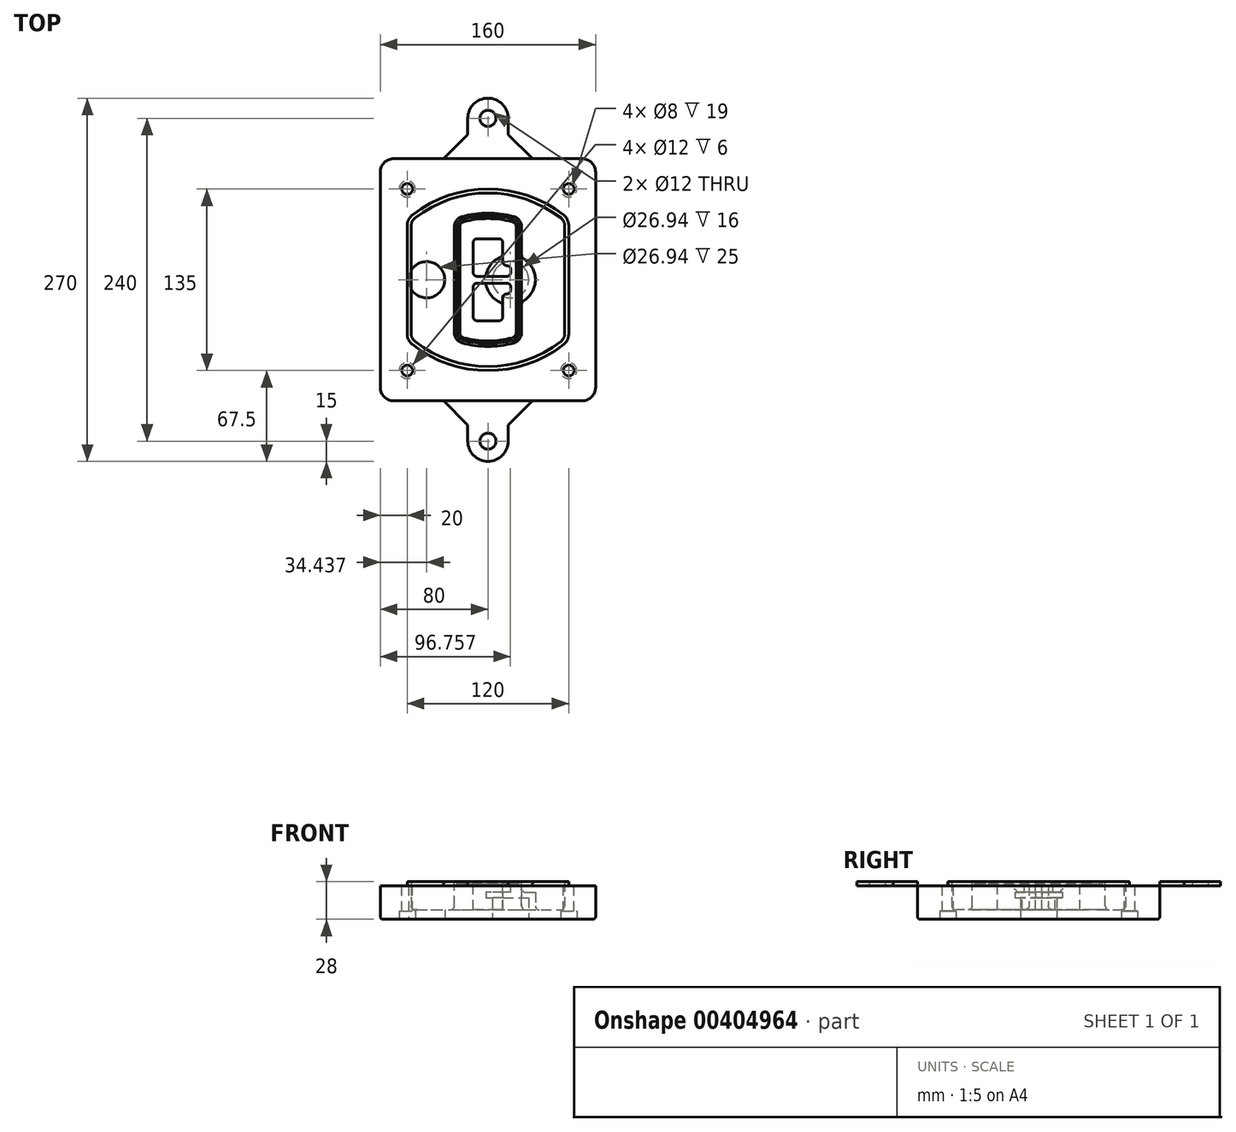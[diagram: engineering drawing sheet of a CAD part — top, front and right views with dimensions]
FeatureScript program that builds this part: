
annotation { "Feature Type Name" : "Feature", "Feature Type Description" : "" }
export const myFeature = defineFeature(function(context is Context, id is Id, definition is map)
    precondition{}
    {
        {
            var Q0;
            Q0=qCreatedBy(makeId("Top.planeOp"),FACE);
            var sketch = newSketch(context, id + "F0", { "sketchPlane" : qUnion([Q0])});
            skPoint(sketch, "E0.rect.middle", {"position": v(0, 0) * mm});
            skLineSegment(sketch, "E1.bottom", {"start": v(-70, -90) * mm, "end": v(70, -90) * mm});
            skLineSegment(sketch, "E1.top", {"start": v(-70, 90) * mm, "end": v(70, 90) * mm});
            skLineSegment(sketch, "E1.left", {"start": v(-80, -80) * mm, "end": v(-80, 80) * mm});
            skLineSegment(sketch, "E1.right", {"start": v(80, -80) * mm, "end": v(80, 80) * mm});
            skLineSegment(sketch, "E2", {"start": v(-80, 90) * mm, "end": v(80, -90) * mm, "construction": true});
            skLineSegment(sketch, "E3", {"start": v(80, 90) * mm, "end": v(-80, -90) * mm, "construction": true});
            skCircle(sketch, "E4", {"center": v(-60, 67.5) * mm, "radius": 4 * mm});
            skCircle(sketch, "E5", {"center": v(60, 67.5) * mm, "radius": 4 * mm});
            skCircle(sketch, "E6", {"center": v(60, -67.5) * mm, "radius": 4 * mm});
            skCircle(sketch, "E7", {"center": v(-60, -67.5) * mm, "radius": 4 * mm});
            skLineSegment(sketch, "E8", {"start": v(-60, 67.5) * mm, "end": v(60, 67.5) * mm, "construction": true});
            skLineSegment(sketch, "E9", {"start": v(60, 67.5) * mm, "end": v(60, -67.5) * mm, "construction": true});
            skLineSegment(sketch, "E10", {"start": v(60, -67.5) * mm, "end": v(-60, -67.5) * mm, "construction": true});
            skLineSegment(sketch, "E11", {"start": v(-60, -67.5) * mm, "end": v(-60, 67.5) * mm, "construction": true});
            skLineSegment(sketch, "E12", {"start": v(-60, 40.3) * mm, "end": v(-60, -40.3) * mm});
            skLineSegment(sketch, "E13", {"start": v(60, 40.3) * mm, "end": v(60, -40.3) * mm});
            skArc(sketch, "E14", {"start": v(56.15, 48.18) * mm, "mid": v(0, 67.5) * mm, "end": v(-56.15, 48.18) * mm});
            skArc(sketch, "E15", {"start": v(-56.15, -48.18) * mm, "mid": v(0, -67.5) * mm, "end": v(56.15, -48.18) * mm});
            skLineSegment(sketch, "E16", {"start": v(-60, 0) * mm, "end": v(60, 0) * mm, "construction": true});
            skPoint(sketch, "E17.visualSharp", {"position": v(-60, -45) * mm});
            skArc(sketch, "E17.filletArc", {"start": v(-60, -40.3) * mm, "mid": v(-58.99, -44.68) * mm, "end": v(-56.15, -48.18) * mm});
            skPoint(sketch, "E18.visualSharp", {"position": v(-60, 45) * mm});
            skArc(sketch, "E18.filletArc", {"start": v(-56.15, 48.18) * mm, "mid": v(-58.99, 44.68) * mm, "end": v(-60, 40.3) * mm});
            skPoint(sketch, "E19.visualSharp", {"position": v(60, 45) * mm});
            skArc(sketch, "E19.filletArc", {"start": v(60, 40.3) * mm, "mid": v(58.99, 44.68) * mm, "end": v(56.15, 48.18) * mm});
            skPoint(sketch, "E20.visualSharp", {"position": v(60, -45) * mm});
            skArc(sketch, "E20.filletArc", {"start": v(56.15, -48.18) * mm, "mid": v(58.99, -44.68) * mm, "end": v(60, -40.3) * mm});
            skPoint(sketch, "E21.visualSharp", {"position": v(-80, 90) * mm});
            skArc(sketch, "E21.filletArc", {"start": v(-70, 90) * mm, "mid": v(-77.07, 87.07) * mm, "end": v(-80, 80) * mm});
            skPoint(sketch, "E22.visualSharp", {"position": v(80, 90) * mm});
            skArc(sketch, "E22.filletArc", {"start": v(80, 80) * mm, "mid": v(77.07, 87.07) * mm, "end": v(70, 90) * mm});
            skPoint(sketch, "E23.visualSharp", {"position": v(80, -90) * mm});
            skArc(sketch, "E23.filletArc", {"start": v(70, -90) * mm, "mid": v(77.07, -87.07) * mm, "end": v(80, -80) * mm});
            skPoint(sketch, "E24.visualSharp", {"position": v(-80, -90) * mm});
            skArc(sketch, "E24.filletArc", {"start": v(-80, -80) * mm, "mid": v(-77.07, -87.07) * mm, "end": v(-70, -90) * mm});
            skArc(sketch, "E25.0", {"start": v(57, 40.3) * mm, "mid": v(56.3, 43.36) * mm, "end": v(54.3, 45.81) * mm});
            skLineSegment(sketch, "E25.1", {"start": v(57, 40.3) * mm, "end": v(57, -40.3) * mm});
            skArc(sketch, "E25.2", {"start": v(54.3, -45.81) * mm, "mid": v(56.3, -43.36) * mm, "end": v(57, -40.3) * mm});
            skArc(sketch, "E25.3", {"start": v(-54.3, -45.81) * mm, "mid": v(0, -64.5) * mm, "end": v(54.3, -45.81) * mm});
            skArc(sketch, "E25.4", {"start": v(-57, -40.3) * mm, "mid": v(-56.3, -43.36) * mm, "end": v(-54.3, -45.81) * mm});
            skArc(sketch, "E25.5", {"start": v(54.3, 45.81) * mm, "mid": v(0, 64.5) * mm, "end": v(-54.3, 45.81) * mm});
            skLineSegment(sketch, "E25.6", {"start": v(-57, 40.3) * mm, "end": v(-57, -40.3) * mm});
            skArc(sketch, "E25.7", {"start": v(-54.3, 45.81) * mm, "mid": v(-56.3, 43.36) * mm, "end": v(-57, 40.3) * mm});
            skArc(sketch, "E26.0", {"start": v(-58.62, 51.33) * mm, "mid": v(-62.58, 46.43) * mm, "end": v(-64, 40.3) * mm});
            skArc(sketch, "E26.1", {"start": v(58.62, 51.33) * mm, "mid": v(0, 71.5) * mm, "end": v(-58.62, 51.33) * mm});
            skArc(sketch, "E26.2", {"start": v(64, 40.3) * mm, "mid": v(62.58, 46.43) * mm, "end": v(58.62, 51.33) * mm});
            skLineSegment(sketch, "E26.3", {"start": v(64, 40.3) * mm, "end": v(64, -40.3) * mm});
            skArc(sketch, "E26.4", {"start": v(58.62, -51.33) * mm, "mid": v(62.58, -46.43) * mm, "end": v(64, -40.3) * mm});
            skLineSegment(sketch, "E26.5", {"start": v(-64, 40.3) * mm, "end": v(-64, -40.3) * mm});
            skArc(sketch, "E26.6", {"start": v(-58.62, -51.33) * mm, "mid": v(0, -71.5) * mm, "end": v(58.62, -51.33) * mm});
            skArc(sketch, "E26.7", {"start": v(-64, -40.3) * mm, "mid": v(-62.58, -46.43) * mm, "end": v(-58.62, -51.33) * mm});
            skSolve(sketch);
        }
        {
            var Q0;
            Q0=makeQuery(id+"F0.imprint","IMPRINT",FACE,{"disambiguationData":[TD([[makeQuery(id+"F0.imprint","IMPRINT",EDGE,{"derivedFrom":sQuery(id+"F0.wireOp",EDGE,"E1.bottom")}),1.0]])]});
            var Q1;
            Q1=makeQuery(id+"F0.imprint","IMPRINT",FACE,{"disambiguationData":[TD([[makeQuery(id+"F0.imprint","IMPRINT",EDGE,{"derivedFrom":sQuery(id+"F0.wireOp",EDGE,"E12")}),1.0]])]});
            var Q2;
            Q2=makeQuery(id+"F0.imprint","IMPRINT",FACE,{"disambiguationData":[TD([[makeQuery(id+"F0.imprint","IMPRINT",EDGE,{"derivedFrom":sQuery(id+"F0.wireOp",EDGE,"E25.0")}),1.0]])]});
            var Q3;
            Q3=makeQuery(id+"F0.imprint","IMPRINT",FACE,{"disambiguationData":[TD([[makeQuery(id+"F0.imprint","IMPRINT",EDGE,{"derivedFrom":sQuery(id+"F0.wireOp",EDGE,"E12")}),-1.0]])]});
            extrude(context, id + "F1", {"entities" : qUnion([Q0, Q1, Q2, Q3]), "oppositeDirection" : true, "depth" : 25 * mm});
        }
        {
            var Q0;
            Q0=makeQuery(id+"F0.imprint","IMPRINT",FACE,{"disambiguationData":[TD([[makeQuery(id+"F0.imprint","IMPRINT",EDGE,{"derivedFrom":sQuery(id+"F0.wireOp",EDGE,"E12")}),1.0]])]});
            extrude(context, id + "F2", {"entities" : qUnion([Q0]), "operationType" : NewBodyOperationType.ADD, "depth" : 3 * mm});
        }
        {
            var Q0;
            Q0=makeQuery(id+"F0.imprint","IMPRINT",FACE,{"disambiguationData":[TD([[makeQuery(id+"F0.imprint","IMPRINT",EDGE,{"derivedFrom":sQuery(id+"F0.wireOp",EDGE,"E25.0")}),1.0]])]});
            extrude(context, id + "F3", {"entities" : qUnion([Q0]), "operationType" : NewBodyOperationType.REMOVE, "oppositeDirection" : true, "depth" : 18 * mm});
        }
        {
            var Q0;
            Q0=makeQuery(id+"F2.opExtrude","CAP_FACE",FACE,{"disambiguationData":[OSD([sQuery(id+"F0.wireOp",EDGE,"E12"),sQuery(id+"F0.wireOp",EDGE,"E13"),sQuery(id+"F0.wireOp",EDGE,"E14"),sQuery(id+"F0.wireOp",EDGE,"E15"),sQuery(id+"F0.wireOp",EDGE,"E17.filletArc"),sQuery(id+"F0.wireOp",EDGE,"E18.filletArc"),sQuery(id+"F0.wireOp",EDGE,"E19.filletArc"),sQuery(id+"F0.wireOp",EDGE,"E20.filletArc"),sQuery(id+"F0.wireOp",EDGE,"E25.0"),sQuery(id+"F0.wireOp",EDGE,"E25.1"),sQuery(id+"F0.wireOp",EDGE,"E25.2"),sQuery(id+"F0.wireOp",EDGE,"E25.3"),sQuery(id+"F0.wireOp",EDGE,"E25.4"),sQuery(id+"F0.wireOp",EDGE,"E25.5"),sQuery(id+"F0.wireOp",EDGE,"E25.6"),sQuery(id+"F0.wireOp",EDGE,"E25.7")])],"isStart":false});
            var sketch = newSketch(context, id + "F4", { "sketchPlane" : qUnion([Q0])});
            skArc(sketch, "E27.0", {"start": v(-19.08, -46.97) * mm, "mid": v(0, -49.5) * mm, "end": v(19.08, -46.97) * mm});
            skArc(sketch, "E28.0", {"start": v(19.08, 46.97) * mm, "mid": v(0, 49.5) * mm, "end": v(-19.08, 46.97) * mm});
            skLineSegment(sketch, "E29", {"start": v(-25, 39.25) * mm, "end": v(-25, -39.25) * mm});
            skLineSegment(sketch, "E30", {"start": v(25, 39.25) * mm, "end": v(25, -39.25) * mm});
            skLineSegment(sketch, "E31", {"start": v(-25, 45.1) * mm, "end": v(25, 45.1) * mm, "construction": true});
            skLineSegment(sketch, "E32", {"start": v(-25, -45.1) * mm, "end": v(25, -45.1) * mm, "construction": true});
            skPoint(sketch, "E33.visualSharp", {"position": v(-25, 45.1) * mm});
            skArc(sketch, "E33.filletArc", {"start": v(-19.08, 46.97) * mm, "mid": v(-23.35, 44.11) * mm, "end": v(-25, 39.25) * mm});
            skPoint(sketch, "E34.visualSharp", {"position": v(25, 45.1) * mm});
            skArc(sketch, "E34.filletArc", {"start": v(25, 39.25) * mm, "mid": v(23.35, 44.11) * mm, "end": v(19.08, 46.97) * mm});
            skPoint(sketch, "E35.visualSharp", {"position": v(25, -45.1) * mm});
            skArc(sketch, "E35.filletArc", {"start": v(19.08, -46.97) * mm, "mid": v(23.35, -44.11) * mm, "end": v(25, -39.25) * mm});
            skPoint(sketch, "E36.visualSharp", {"position": v(-25, -45.1) * mm});
            skArc(sketch, "E36.filletArc", {"start": v(-25, -39.25) * mm, "mid": v(-23.35, -44.11) * mm, "end": v(-19.08, -46.97) * mm});
            skArc(sketch, "E37.0", {"start": v(54.3, 45.81) * mm, "mid": v(0, 64.5) * mm, "end": v(-54.3, 45.81) * mm});
            skArc(sketch, "E37.1", {"start": v(-54.3, 45.81) * mm, "mid": v(-56.3, 43.36) * mm, "end": v(-57, 40.3) * mm});
            skLineSegment(sketch, "E37.2", {"start": v(-57, 40.3) * mm, "end": v(-57, -40.3) * mm});
            skArc(sketch, "E37.3", {"start": v(-57, -40.3) * mm, "mid": v(-56.3, -43.36) * mm, "end": v(-54.3, -45.81) * mm});
            skArc(sketch, "E37.4", {"start": v(-54.3, -45.81) * mm, "mid": v(0, -64.5) * mm, "end": v(54.3, -45.81) * mm});
            skArc(sketch, "E37.5", {"start": v(54.3, -45.81) * mm, "mid": v(56.3, -43.36) * mm, "end": v(57, -40.3) * mm});
            skLineSegment(sketch, "E37.6", {"start": v(57, 40.3) * mm, "end": v(57, -40.3) * mm});
            skArc(sketch, "E37.7", {"start": v(57, 40.3) * mm, "mid": v(56.3, 43.36) * mm, "end": v(54.3, 45.81) * mm});
            skLineSegment(sketch, "E38.0", {"start": v(23, 39.25) * mm, "end": v(23, -39.25) * mm});
            skArc(sketch, "E38.1", {"start": v(18.56, -45.04) * mm, "mid": v(21.76, -42.9) * mm, "end": v(23, -39.25) * mm});
            skArc(sketch, "E38.2", {"start": v(-18.56, -45.04) * mm, "mid": v(0, -47.5) * mm, "end": v(18.56, -45.04) * mm});
            skArc(sketch, "E38.3", {"start": v(-23, -39.25) * mm, "mid": v(-21.76, -42.9) * mm, "end": v(-18.56, -45.04) * mm});
            skLineSegment(sketch, "E38.4", {"start": v(-23, 39.25) * mm, "end": v(-23, -39.25) * mm});
            skArc(sketch, "E38.5", {"start": v(23, 39.25) * mm, "mid": v(21.76, 42.9) * mm, "end": v(18.56, 45.04) * mm});
            skArc(sketch, "E38.6", {"start": v(-18.56, 45.04) * mm, "mid": v(-21.76, 42.9) * mm, "end": v(-23, 39.25) * mm});
            skArc(sketch, "E38.7", {"start": v(18.56, 45.04) * mm, "mid": v(0, 47.5) * mm, "end": v(-18.56, 45.04) * mm});
            skArc(sketch, "E39.0", {"start": v(21, 39.25) * mm, "mid": v(20.18, 41.68) * mm, "end": v(18.04, 43.1) * mm});
            skLineSegment(sketch, "E39.1", {"start": v(21, 39.25) * mm, "end": v(21, -39.25) * mm});
            skArc(sketch, "E39.2", {"start": v(18.04, -43.1) * mm, "mid": v(20.18, -41.68) * mm, "end": v(21, -39.25) * mm});
            skArc(sketch, "E39.3", {"start": v(-18.04, -43.1) * mm, "mid": v(0, -45.5) * mm, "end": v(18.04, -43.1) * mm});
            skArc(sketch, "E39.4", {"start": v(-21, -39.25) * mm, "mid": v(-20.18, -41.68) * mm, "end": v(-18.04, -43.1) * mm});
            skArc(sketch, "E39.5", {"start": v(18.04, 43.1) * mm, "mid": v(0, 45.5) * mm, "end": v(-18.04, 43.1) * mm});
            skLineSegment(sketch, "E39.6", {"start": v(-21, 39.25) * mm, "end": v(-21, -39.25) * mm});
            skArc(sketch, "E39.7", {"start": v(-18.04, 43.1) * mm, "mid": v(-20.18, 41.68) * mm, "end": v(-21, 39.25) * mm});
            skLineSegment(sketch, "E40", {"start": v(-25, 0) * mm, "end": v(25, 0) * mm, "construction": true});
            skLineSegment(sketch, "E41", {"start": v(-11, 5.5) * mm, "end": v(-11, 27.5) * mm});
            skLineSegment(sketch, "E42", {"start": v(-8, 30.5) * mm, "end": v(8, 30.5) * mm});
            skLineSegment(sketch, "E43", {"start": v(11, 27.5) * mm, "end": v(11, 13.5) * mm});
            skLineSegment(sketch, "E44", {"start": v(14, 10.5) * mm, "end": v(14, 10.5) * mm});
            skLineSegment(sketch, "E45", {"start": v(17, 7.5) * mm, "end": v(17, 5.5) * mm});
            skLineSegment(sketch, "E46", {"start": v(14, 2.5) * mm, "end": v(-8, 2.5) * mm});
            skPoint(sketch, "E47.visualSharp", {"position": v(-11, 30.5) * mm});
            skArc(sketch, "E47.filletArc", {"start": v(-8, 30.5) * mm, "mid": v(-10.12, 29.62) * mm, "end": v(-11, 27.5) * mm});
            skPoint(sketch, "E48.visualSharp", {"position": v(11, 30.5) * mm});
            skArc(sketch, "E48.filletArc", {"start": v(11, 27.5) * mm, "mid": v(10.12, 29.62) * mm, "end": v(8, 30.5) * mm});
            skPoint(sketch, "E49.visualSharp", {"position": v(11, 10.5) * mm});
            skArc(sketch, "E49.filletArc", {"start": v(11, 13.5) * mm, "mid": v(11.88, 11.38) * mm, "end": v(14, 10.5) * mm});
            skPoint(sketch, "E50.visualSharp", {"position": v(17, 10.5) * mm});
            skArc(sketch, "E50.filletArc", {"start": v(17, 7.5) * mm, "mid": v(16.12, 9.62) * mm, "end": v(14, 10.5) * mm});
            skPoint(sketch, "E51.visualSharp", {"position": v(17, 2.5) * mm});
            skArc(sketch, "E51.filletArc", {"start": v(14, 2.5) * mm, "mid": v(16.12, 3.38) * mm, "end": v(17, 5.5) * mm});
            skPoint(sketch, "E52.visualSharp", {"position": v(-11, 2.5) * mm});
            skArc(sketch, "E52.filletArc", {"start": v(-11, 5.5) * mm, "mid": v(-10.12, 3.38) * mm, "end": v(-8, 2.5) * mm});
            skLineSegment(sketch, "E53.0.MirrorCS", {"start": v(14, -2.5) * mm, "end": v(-8, -2.5) * mm});
            skArc(sketch, "E54.0.MirrorCS", {"start": v(-11, -5.5) * mm, "mid": v(-10.12, -3.38) * mm, "end": v(-8, -2.5) * mm});
            skLineSegment(sketch, "E55.0.MirrorCS", {"start": v(-11, -5.5) * mm, "end": v(-11, -27.5) * mm});
            skArc(sketch, "E56.0.MirrorCS", {"start": v(-8, -30.5) * mm, "mid": v(-10.12, -29.62) * mm, "end": v(-11, -27.5) * mm});
            skLineSegment(sketch, "E57.0.MirrorCS", {"start": v(-8, -30.5) * mm, "end": v(8, -30.5) * mm});
            skArc(sketch, "E58.0.MirrorCS", {"start": v(11, -27.5) * mm, "mid": v(10.12, -29.62) * mm, "end": v(8, -30.5) * mm});
            skLineSegment(sketch, "E59.0.MirrorCS", {"start": v(11, -27.5) * mm, "end": v(11, -13.5) * mm});
            skArc(sketch, "E60.0.MirrorCS", {"start": v(11, -13.5) * mm, "mid": v(11.88, -11.38) * mm, "end": v(14, -10.5) * mm});
            skArc(sketch, "E61.0.MirrorCS", {"start": v(17, -7.5) * mm, "mid": v(16.12, -9.62) * mm, "end": v(14, -10.5) * mm});
            skLineSegment(sketch, "E62.0.MirrorCS", {"start": v(17, -7.5) * mm, "end": v(17, -5.5) * mm});
            skArc(sketch, "E63.0.MirrorCS", {"start": v(14, -2.5) * mm, "mid": v(16.12, -3.38) * mm, "end": v(17, -5.5) * mm});
            skSolve(sketch);
        }
        {
            var Q0;
            Q0=makeQuery(id+"F4.imprint","IMPRINT",FACE,{"disambiguationData":[TD([[makeQuery(id+"F4.imprint","IMPRINT",EDGE,{"derivedFrom":sQuery(id+"F4.wireOp",EDGE,"E27.0")}),1.0]])]});
            var Q1;
            Q1=makeQuery(id+"F4.imprint","IMPRINT",FACE,{"disambiguationData":[TD([[makeQuery(id+"F4.imprint","IMPRINT",EDGE,{"derivedFrom":sQuery(id+"F4.wireOp",EDGE,"E38.0")}),-1.0]])]});
            var Q2;
            Q2=makeQuery(id+"F4.imprint","IMPRINT",FACE,{"disambiguationData":[TD([[makeQuery(id+"F4.imprint","IMPRINT",EDGE,{"derivedFrom":sQuery(id+"F4.wireOp",EDGE,"E39.0")}),1.0]])]});
            extrude(context, id + "F5", {"entities" : qUnion([Q0, Q1, Q2]), "operationType" : NewBodyOperationType.ADD, "endBound" : BoundingType.UP_TO_NEXT, "oppositeDirection" : true, "depth" : 25 * mm});
        }
        {
            var Q0;
            Q0=makeQuery(id+"F4.imprint","IMPRINT",FACE,{"disambiguationData":[TD([[makeQuery(id+"F4.imprint","IMPRINT",EDGE,{"derivedFrom":sQuery(id+"F4.wireOp",EDGE,"E38.0")}),-1.0]])]});
            extrude(context, id + "F6", {"entities" : qUnion([Q0]), "operationType" : NewBodyOperationType.REMOVE, "oppositeDirection" : true, "depth" : 2 * mm});
        }
        {
            var Q0;
            Q0=makeQuery(id+"F1.opExtrude","CAP_FACE",FACE,{"disambiguationData":[OSD([sQuery(id+"F0.wireOp",EDGE,"E1.bottom"),sQuery(id+"F0.wireOp",EDGE,"E1.top"),sQuery(id+"F0.wireOp",EDGE,"E1.left"),sQuery(id+"F0.wireOp",EDGE,"E1.right"),sQuery(id+"F0.wireOp",EDGE,"E4"),sQuery(id+"F0.wireOp",EDGE,"E5"),sQuery(id+"F0.wireOp",EDGE,"E6"),sQuery(id+"F0.wireOp",EDGE,"E7"),sQuery(id+"F0.wireOp",EDGE,"E21.filletArc"),sQuery(id+"F0.wireOp",EDGE,"E22.filletArc"),sQuery(id+"F0.wireOp",EDGE,"E23.filletArc"),sQuery(id+"F0.wireOp",EDGE,"E24.filletArc")])],"isStart":false});
            var sketch = newSketch(context, id + "F7", { "sketchPlane" : qUnion([Q0])});
            skCircle(sketch, "E64", {"center": v(16.76, 0) * mm, "radius": 13.47 * mm});
            skCircle(sketch, "E65", {"center": v(-45.56, 0) * mm, "radius": 13.47 * mm});
            skLineSegment(sketch, "E66", {"start": v(80, 0) * mm, "end": v(-80, 0) * mm});
            skCircle(sketch, "E67", {"center": v(16.76, 0) * mm, "radius": 18.47 * mm});
            skCircle(sketch, "E68", {"center": v(60, -67.5) * mm, "radius": 6 * mm});
            skCircle(sketch, "E69", {"center": v(-60, -67.5) * mm, "radius": 6 * mm});
            skCircle(sketch, "E70", {"center": v(-60, 67.5) * mm, "radius": 6 * mm});
            skCircle(sketch, "E71", {"center": v(60, 67.5) * mm, "radius": 6 * mm});
            skSolve(sketch);
        }
        {
            var Q0;
            {var subQ1=sQuery(id+"F7.wireOp",EDGE,"E66");var subQ4=sQuery(id+"F7.wireOp",EDGE,"E64");var subQ6=makeQuery(id+"F7.imprint","INTERSECT",VERTEX,{"disambiguationData":[OD(0.0)],"derivedFrom":[subQ4,subQ1]});Q0=makeQuery(id+"F7.imprint","IMPRINT",FACE,{"disambiguationData":[TD([[makeQuery(id+"F7.imprint","IMPRINT",EDGE,{"disambiguationData":[TD([[subQ6,-1.0]])],"derivedFrom":subQ4}),-1.0]])]});}
            var Q1;
            {var subQ0=sQuery(id+"F7.wireOp",EDGE,"E66");var subQ1=sQuery(id+"F7.wireOp",EDGE,"E64");var subQ3=makeQuery(id+"F7.imprint","INTERSECT",VERTEX,{"disambiguationData":[OD(0.0)],"derivedFrom":[subQ1,subQ0]});Q1=makeQuery(id+"F7.imprint","IMPRINT",FACE,{"disambiguationData":[TD([[makeQuery(id+"F7.imprint","IMPRINT",EDGE,{"disambiguationData":[TD([[subQ3,-1.0]])],"derivedFrom":subQ1}),1.0]])]});}
            var Q2;
            {var subQ0=sQuery(id+"F7.wireOp",EDGE,"E66");var subQ1=sQuery(id+"F7.wireOp",EDGE,"E64");var subQ3=makeQuery(id+"F7.imprint","INTERSECT",VERTEX,{"disambiguationData":[OD(0.0)],"derivedFrom":[subQ1,subQ0]});Q2=makeQuery(id+"F7.imprint","IMPRINT",FACE,{"disambiguationData":[TD([[makeQuery(id+"F7.imprint","IMPRINT",EDGE,{"disambiguationData":[TD([[subQ3,1.0]])],"derivedFrom":subQ1}),1.0]])]});}
            var Q3;
            {var subQ1=sQuery(id+"F7.wireOp",EDGE,"E66");var subQ4=sQuery(id+"F7.wireOp",EDGE,"E64");var subQ6=makeQuery(id+"F7.imprint","INTERSECT",VERTEX,{"disambiguationData":[OD(0.0)],"derivedFrom":[subQ4,subQ1]});Q3=makeQuery(id+"F7.imprint","IMPRINT",FACE,{"disambiguationData":[TD([[makeQuery(id+"F7.imprint","IMPRINT",EDGE,{"disambiguationData":[TD([[subQ6,1.0]])],"derivedFrom":subQ4}),-1.0]])]});}
            extrude(context, id + "F8", {"entities" : qUnion([Q0, Q1, Q2, Q3]), "operationType" : NewBodyOperationType.ADD, "oppositeDirection" : true, "depth" : 20 * mm});
        }
        {
            var Q0;
            {var subQ0=sQuery(id+"F7.wireOp",EDGE,"E66");var subQ1=sQuery(id+"F7.wireOp",EDGE,"E64");var subQ3=makeQuery(id+"F7.imprint","INTERSECT",VERTEX,{"disambiguationData":[OD(0.0)],"derivedFrom":[subQ1,subQ0]});Q0=makeQuery(id+"F7.imprint","IMPRINT",FACE,{"disambiguationData":[TD([[makeQuery(id+"F7.imprint","IMPRINT",EDGE,{"disambiguationData":[TD([[subQ3,-1.0]])],"derivedFrom":subQ1}),1.0]])]});}
            var Q1;
            {var subQ0=sQuery(id+"F7.wireOp",EDGE,"E66");var subQ1=sQuery(id+"F7.wireOp",EDGE,"E64");var subQ3=makeQuery(id+"F7.imprint","INTERSECT",VERTEX,{"disambiguationData":[OD(0.0)],"derivedFrom":[subQ1,subQ0]});Q1=makeQuery(id+"F7.imprint","IMPRINT",FACE,{"disambiguationData":[TD([[makeQuery(id+"F7.imprint","IMPRINT",EDGE,{"disambiguationData":[TD([[subQ3,1.0]])],"derivedFrom":subQ1}),1.0]])]});}
            extrude(context, id + "F9", {"entities" : qUnion([Q0, Q1]), "operationType" : NewBodyOperationType.REMOVE, "oppositeDirection" : true, "depth" : 16 * mm});
        }
        {
            var Q0;
            {var subQ0=sQuery(id+"F7.wireOp",EDGE,"E66");var subQ1=sQuery(id+"F7.wireOp",EDGE,"E65");var subQ3=makeQuery(id+"F7.imprint","INTERSECT",VERTEX,{"disambiguationData":[OD(0.0)],"derivedFrom":[subQ1,subQ0]});Q0=makeQuery(id+"F7.imprint","IMPRINT",FACE,{"disambiguationData":[TD([[makeQuery(id+"F7.imprint","IMPRINT",EDGE,{"disambiguationData":[TD([[subQ3,-1.0]])],"derivedFrom":subQ1}),1.0]])]});}
            var Q1;
            {var subQ0=sQuery(id+"F7.wireOp",EDGE,"E66");var subQ1=sQuery(id+"F7.wireOp",EDGE,"E65");var subQ3=makeQuery(id+"F7.imprint","INTERSECT",VERTEX,{"disambiguationData":[OD(0.0)],"derivedFrom":[subQ1,subQ0]});Q1=makeQuery(id+"F7.imprint","IMPRINT",FACE,{"disambiguationData":[TD([[makeQuery(id+"F7.imprint","IMPRINT",EDGE,{"disambiguationData":[TD([[subQ3,1.0]])],"derivedFrom":subQ1}),1.0]])]});}
            extrude(context, id + "F10", {"entities" : qUnion([Q0, Q1]), "operationType" : NewBodyOperationType.REMOVE, "oppositeDirection" : true, "depth" : 25 * mm});
        }
        {
            var Q0;
            Q0=makeQuery(id+"F7.imprint","IMPRINT",FACE,{"disambiguationData":[TD([[makeQuery(id+"F7.imprint","IMPRINT",EDGE,{"derivedFrom":sQuery(id+"F7.wireOp",EDGE,"E68")}),1.0]])]});
            var Q1;
            Q1=makeQuery(id+"F7.imprint","IMPRINT",FACE,{"disambiguationData":[TD([[makeQuery(id+"F7.imprint","IMPRINT",EDGE,{"derivedFrom":makeQuery(id+"F1.opExtrude","CAP_EDGE",EDGE,{"disambiguationData":[OSD([sQuery(id+"F0.wireOp",EDGE,"E5")])],"isStart":false})}),-1.0]])]});
            var Q2;
            Q2=makeQuery(id+"F7.imprint","IMPRINT",FACE,{"disambiguationData":[TD([[makeQuery(id+"F7.imprint","IMPRINT",EDGE,{"derivedFrom":sQuery(id+"F7.wireOp",EDGE,"E69")}),1.0]])]});
            var Q3;
            Q3=makeQuery(id+"F7.imprint","IMPRINT",FACE,{"disambiguationData":[TD([[makeQuery(id+"F7.imprint","IMPRINT",EDGE,{"derivedFrom":makeQuery(id+"F1.opExtrude","CAP_EDGE",EDGE,{"disambiguationData":[OSD([sQuery(id+"F0.wireOp",EDGE,"E4")])],"isStart":false})}),-1.0]])]});
            var Q4;
            Q4=makeQuery(id+"F7.imprint","IMPRINT",FACE,{"disambiguationData":[TD([[makeQuery(id+"F7.imprint","IMPRINT",EDGE,{"derivedFrom":sQuery(id+"F7.wireOp",EDGE,"E70")}),1.0]])]});
            var Q5;
            Q5=makeQuery(id+"F7.imprint","IMPRINT",FACE,{"disambiguationData":[TD([[makeQuery(id+"F7.imprint","IMPRINT",EDGE,{"derivedFrom":makeQuery(id+"F1.opExtrude","CAP_EDGE",EDGE,{"disambiguationData":[OSD([sQuery(id+"F0.wireOp",EDGE,"E7")])],"isStart":false})}),-1.0]])]});
            var Q6;
            Q6=makeQuery(id+"F7.imprint","IMPRINT",FACE,{"disambiguationData":[TD([[makeQuery(id+"F7.imprint","IMPRINT",EDGE,{"derivedFrom":sQuery(id+"F7.wireOp",EDGE,"E71")}),1.0]])]});
            var Q7;
            Q7=makeQuery(id+"F7.imprint","IMPRINT",FACE,{"disambiguationData":[TD([[makeQuery(id+"F7.imprint","IMPRINT",EDGE,{"derivedFrom":makeQuery(id+"F1.opExtrude","CAP_EDGE",EDGE,{"disambiguationData":[OSD([sQuery(id+"F0.wireOp",EDGE,"E6")])],"isStart":false})}),-1.0]])]});
            extrude(context, id + "F11", {"entities" : qUnion([Q0, Q1, Q2, Q3, Q4, Q5, Q6, Q7]), "operationType" : NewBodyOperationType.REMOVE, "oppositeDirection" : true, "depth" : 6 * mm});
        }
        {
            var Q0;
            Q0=makeQuery(id+"F9.boolean.opBoolean","COPY",FACE,{"derivedFrom":makeQuery(id+"F9.opExtrude","CAP_FACE",FACE,{"disambiguationData":[OSD([sQuery(id+"F7.wireOp",EDGE,"E64")])],"isStart":false})});
            var sketch = newSketch(context, id + "F12", { "sketchPlane" : qUnion([Q0])});
            skArc(sketch, "E72.0", {"start": v(11, 17.55) * mm, "mid": v(2.57, 11.82) * mm, "end": v(-1.54, 2.5) * mm});
            skArc(sketch, "E72.1", {"start": v(-1.54, -2.5) * mm, "mid": v(2.57, -11.82) * mm, "end": v(11, -17.55) * mm});
            skLineSegment(sketch, "E73", {"start": v(-1.54, -2.5) * mm, "end": v(14, -2.5) * mm});
            skLineSegment(sketch, "E74.0", {"start": v(14, 2.5) * mm, "end": v(-1.54, 2.5) * mm});
            skArc(sketch, "E74.1", {"start": v(14, 2.5) * mm, "mid": v(16.12, 3.38) * mm, "end": v(17, 5.5) * mm});
            skLineSegment(sketch, "E74.2", {"start": v(17, 7.5) * mm, "end": v(17, 5.5) * mm});
            skArc(sketch, "E74.3", {"start": v(17, 7.5) * mm, "mid": v(16.12, 9.62) * mm, "end": v(14, 10.5) * mm});
            skArc(sketch, "E74.4", {"start": v(11, 13.5) * mm, "mid": v(11.88, 11.38) * mm, "end": v(14, 10.5) * mm});
            skLineSegment(sketch, "E74.5", {"start": v(11, 17.55) * mm, "end": v(11, 13.5) * mm});
            skLineSegment(sketch, "E74.7", {"start": v(14, -2.5) * mm, "end": v(-1.54, -2.5) * mm});
            skArc(sketch, "E74.8", {"start": v(14, -2.5) * mm, "mid": v(16.12, -3.38) * mm, "end": v(17, -5.5) * mm});
            skLineSegment(sketch, "E74.9", {"start": v(17, -7.5) * mm, "end": v(17, -5.5) * mm});
            skArc(sketch, "E74.10", {"start": v(17, -7.5) * mm, "mid": v(16.12, -9.62) * mm, "end": v(14, -10.5) * mm});
            skArc(sketch, "E74.11", {"start": v(11, -13.5) * mm, "mid": v(11.88, -11.38) * mm, "end": v(14, -10.5) * mm});
            skLineSegment(sketch, "E74.12", {"start": v(11, -17.55) * mm, "end": v(11, -13.5) * mm});
            skPoint(sketch, "E75.orphan", {"position": v(11, -27.5) * mm});
            skPoint(sketch, "E76.orphan", {"position": v(-8, -2.5) * mm});
            skPoint(sketch, "E77.orphan", {"position": v(-8, 2.5) * mm});
            skPoint(sketch, "E78.orphan", {"position": v(11, 27.5) * mm});
            skSolve(sketch);
        }
        {
            var Q0;
            {var subQ7=sQuery(id+"F12.wireOp",EDGE,"E72.0");var subQ14=sQuery(id+"F12.wireOp",EDGE,"E72.1");var subQ16=sQuery(id+"F12.wireOp",EDGE,"E74.1");var subQ18=sQuery(id+"F12.wireOp",EDGE,"E74.8");Q0=qUnion([makeQuery(id+"F12.imprint","IMPRINT",FACE,{"disambiguationData":[TD([[makeQuery(id+"F12.imprint","IMPRINT",EDGE,{"derivedFrom":subQ7}),1.0]])]}),makeQuery(id+"F12.imprint","IMPRINT",FACE,{"disambiguationData":[TD([[makeQuery(id+"F12.imprint","IMPRINT",EDGE,{"derivedFrom":subQ14}),1.0]])]}),makeQuery(id+"F12.imprint","IMPRINT",FACE,{"disambiguationData":[TD([[makeQuery(id+"F12.imprint","IMPRINT",EDGE,{"derivedFrom":subQ16}),1.0]])]}),makeQuery(id+"F12.imprint","IMPRINT",FACE,{"disambiguationData":[TD([[makeQuery(id+"F12.imprint","IMPRINT",EDGE,{"derivedFrom":subQ18}),-1.0]])]})]);}
            var Q1;
            Q1=makeQuery(id+"F5.boolean.opBoolean","SPLIT",FACE,{"disambiguationData":[TD([makeQuery(id+"F5.opExtrude","SWEPT_FACE",FACE,{"disambiguationData":[OSD([sQuery(id+"F4.wireOp",EDGE,"E41")])]})])],"derivedFrom":makeQuery(id+"F3.boolean.opBoolean","COPY",FACE,{"derivedFrom":makeQuery(id+"F3.opExtrude","CAP_FACE",FACE,{"disambiguationData":[OSD([sQuery(id+"F0.wireOp",EDGE,"E25.0"),sQuery(id+"F0.wireOp",EDGE,"E25.1"),sQuery(id+"F0.wireOp",EDGE,"E25.2"),sQuery(id+"F0.wireOp",EDGE,"E25.3"),sQuery(id+"F0.wireOp",EDGE,"E25.4"),sQuery(id+"F0.wireOp",EDGE,"E25.5"),sQuery(id+"F0.wireOp",EDGE,"E25.6"),sQuery(id+"F0.wireOp",EDGE,"E25.7")])],"isStart":false})})});
            extrude(context, id + "F13", {"entities" : qUnion([Q0]), "operationType" : NewBodyOperationType.REMOVE, "endBound" : BoundingType.UP_TO_SURFACE, "endBoundEntityFace" : qUnion([Q1]), "depth" : 25 * mm});
        }
        {
            var Q0;
            Q0=makeQuery(id+"F3.boolean.opBoolean","COPY",EDGE,{"derivedFrom":makeQuery(id+"F3.opExtrude","CAP_EDGE",EDGE,{"disambiguationData":[OSD([sQuery(id+"F0.wireOp",EDGE,"E25.6")])],"isStart":false})});
            var Q1;
            Q1=makeQuery(id+"F8.boolean.opBoolean","INTERSECT",EDGE,{"derivedFrom":[makeQuery(id+"F5.opExtrude","SWEPT_FACE",FACE,{"disambiguationData":[OSD([sQuery(id+"F4.wireOp",EDGE,"E30")])]}),makeQuery(id+"F8.opExtrude","CAP_FACE",FACE,{"disambiguationData":[OSD([sQuery(id+"F7.wireOp",EDGE,"E67")])],"isStart":false})]});
            var Q2;
            Q2=makeQuery(id+"F8.boolean.opBoolean","INTERSECT",EDGE,{"disambiguationData":[OD(1.0)],"derivedFrom":[makeQuery(id+"F5.opExtrude","SWEPT_FACE",FACE,{"disambiguationData":[OSD([sQuery(id+"F4.wireOp",EDGE,"E30")])]}),makeQuery(id+"F8.opExtrude","SWEPT_FACE",FACE,{"disambiguationData":[OSD([sQuery(id+"F7.wireOp",EDGE,"E67")])]})]});
            var Q3;
            {var subQ0=sQuery(id+"F4.wireOp",EDGE,"E30");Q3=makeQuery(id+"F8.boolean.opBoolean","SPLIT",EDGE,{"disambiguationData":[TD([makeQuery(id+"F5.opExtrude","SWEPT_FACE",FACE,{"disambiguationData":[OSD([sQuery(id+"F4.wireOp",EDGE,"E35.filletArc")])]})])],"derivedFrom":makeQuery(id+"F5.opExtrude","CAP_EDGE",EDGE,{"disambiguationData":[OSD([subQ0])],"isStart":false})});}
            var Q4;
            {var subQ0=sQuery(id+"F0.wireOp",EDGE,"E25.7");var subQ1=sQuery(id+"F0.wireOp",EDGE,"E25.1");var subQ2=sQuery(id+"F0.wireOp",EDGE,"E25.6");var subQ3=sQuery(id+"F0.wireOp",EDGE,"E25.5");var subQ4=sQuery(id+"F0.wireOp",EDGE,"E25.4");var subQ5=sQuery(id+"F0.wireOp",EDGE,"E25.0");var subQ6=sQuery(id+"F0.wireOp",EDGE,"E25.2");var subQ7=sQuery(id+"F0.wireOp",EDGE,"E25.3");Q4=makeQuery(id+"F8.boolean.opBoolean","INTERSECT",EDGE,{"derivedFrom":[makeQuery(id+"F5.boolean.opBoolean","SPLIT",FACE,{"disambiguationData":[TD([makeQuery(id+"F2.opExtrude","SWEPT_FACE",FACE,{"disambiguationData":[OSD([subQ5])]})])],"derivedFrom":makeQuery(id+"F3.boolean.opBoolean","COPY",FACE,{"derivedFrom":makeQuery(id+"F3.opExtrude","CAP_FACE",FACE,{"disambiguationData":[OSD([subQ5,subQ1,subQ6,subQ7,subQ4,subQ3,subQ2,subQ0])],"isStart":false})})}),makeQuery(id+"F8.opExtrude","SWEPT_FACE",FACE,{"disambiguationData":[OSD([sQuery(id+"F7.wireOp",EDGE,"E67")])]})]});}
            var Q5;
            Q5=makeQuery(id+"F8.boolean.opBoolean","INTERSECT",EDGE,{"disambiguationData":[OD(0.0)],"derivedFrom":[makeQuery(id+"F5.opExtrude","SWEPT_FACE",FACE,{"disambiguationData":[OSD([sQuery(id+"F4.wireOp",EDGE,"E30")])]}),makeQuery(id+"F8.opExtrude","SWEPT_FACE",FACE,{"disambiguationData":[OSD([sQuery(id+"F7.wireOp",EDGE,"E67")])]})]});
            fillet(context, id + "F14", {"entities" : qUnion([Q0, Q1, Q2, Q3, Q4, Q5]), "radius" : 3 * mm, "tangentPropagation" : true, "allowEdgeOverflow" : false});
        }
        {
            var Q0;
            Q0=makeQuery(id+"F1.opExtrude","CAP_EDGE",EDGE,{"disambiguationData":[OSD([sQuery(id+"F0.wireOp",EDGE,"E1.bottom")])],"isStart":false});
            fillet(context, id + "F15", {"entities" : qUnion([Q0]), "radius" : 2 * mm, "tangentPropagation" : true, "allowEdgeOverflow" : false});
        }
        {
            var Q0;
            {var subQ0=sQuery(id+"F0.wireOp",EDGE,"E21.filletArc");var subQ1=sQuery(id+"F0.wireOp",EDGE,"E7");var subQ2=sQuery(id+"F0.wireOp",EDGE,"E6");var subQ3=sQuery(id+"F0.wireOp",EDGE,"E5");var subQ4=sQuery(id+"F0.wireOp",EDGE,"E4");var subQ5=sQuery(id+"F0.wireOp",EDGE,"E22.filletArc");var subQ6=sQuery(id+"F0.wireOp",EDGE,"E1.bottom");var subQ7=sQuery(id+"F0.wireOp",EDGE,"E1.right");var subQ8=sQuery(id+"F0.wireOp",EDGE,"E1.top");var subQ9=sQuery(id+"F0.wireOp",EDGE,"E1.left");var subQ10=sQuery(id+"F0.wireOp",EDGE,"E23.filletArc");var subQ11=sQuery(id+"F0.wireOp",EDGE,"E24.filletArc");Q0=makeQuery(id+"F2.boolean.opBoolean","SPLIT",FACE,{"disambiguationData":[TD([makeQuery(id+"F1.opExtrude","SWEPT_FACE",FACE,{"disambiguationData":[OSD([subQ6])]})])],"derivedFrom":makeQuery(id+"F1.opExtrude","CAP_FACE",FACE,{"disambiguationData":[OSD([subQ6,subQ8,subQ9,subQ7,subQ4,subQ3,subQ2,subQ1,subQ0,subQ5,subQ10,subQ11])],"isStart":true})});}
            var sketch = newSketch(context, id + "F16", { "sketchPlane" : qUnion([Q0])});
            skLineSegment(sketch, "E79", {"start": v(0, 90) * mm, "end": v(0, 120) * mm, "construction": true});
            skCircle(sketch, "E80", {"center": v(0, 120) * mm, "radius": 6 * mm});
            skLineSegment(sketch, "E81", {"start": v(-33, 90) * mm, "end": v(-15, 108) * mm});
            skLineSegment(sketch, "E82", {"start": v(-15, 108) * mm, "end": v(-15, 120) * mm});
            skArc(sketch, "E83", {"start": v(15, 120) * mm, "mid": v(0, 135) * mm, "end": v(-15, 120) * mm});
            skLineSegment(sketch, "E84", {"start": v(15, 120) * mm, "end": v(15, 108) * mm});
            skLineSegment(sketch, "E85", {"start": v(15, 108) * mm, "end": v(33, 90) * mm});
            skLineSegment(sketch, "E86", {"start": v(-80, 0) * mm, "end": v(80, 0) * mm, "construction": true});
            skLineSegment(sketch, "E87.MirrorCS", {"start": v(15, -120) * mm, "end": v(15, -108) * mm});
            skArc(sketch, "E88.MirrorCS", {"start": v(15, -120) * mm, "mid": v(0, -135) * mm, "end": v(-15, -120) * mm});
            skLineSegment(sketch, "E89.MirrorCS", {"start": v(15, -108) * mm, "end": v(33, -90) * mm});
            skLineSegment(sketch, "E90.MirrorCS", {"start": v(0, -90) * mm, "end": v(0, -120) * mm, "construction": true});
            skCircle(sketch, "E91.MirrorC", {"center": v(0, -120) * mm, "radius": 6 * mm});
            skLineSegment(sketch, "E92.MirrorCS", {"start": v(-33, -90) * mm, "end": v(-15, -108) * mm});
            skLineSegment(sketch, "E93.MirrorCS", {"start": v(-15, -108) * mm, "end": v(-15, -120) * mm});
            skSolve(sketch);
        }
        {
            var Q0;
            {var subQ5=sQuery(id+"F16.wireOp",EDGE,"H8i3Y212-Wiv2-OnTc-ds8V-wbEU4xrU6Obw");Q0=makeQuery(id+"F16.imprint","IMPRINT",FACE,{"disambiguationData":[TD([[makeQuery(id+"F16.imprint","IMPRINT",EDGE,{"derivedFrom":subQ5}),-1.0]])]});}
            var Q1;
            Q1=makeQuery(id+"F16.imprint","IMPRINT",FACE,{"disambiguationData":[TD([[makeQuery(id+"F16.imprint","IMPRINT",EDGE,{"derivedFrom":sQuery(id+"F16.wireOp",EDGE,"E80")}),-1.0]])]});
            var Q2;
            Q2=makeQuery(id+"F16.imprint","IMPRINT",FACE,{"disambiguationData":[TD([[makeQuery(id+"F16.imprint","IMPRINT",EDGE,{"derivedFrom":sQuery(id+"F16.wireOp",EDGE,"E87.MirrorCS")}),1.0]])]});
            var Q3;
            Q3=makeQuery(id+"F2.opExtrude","CAP_FACE",FACE,{"disambiguationData":[OSD([sQuery(id+"F0.wireOp",EDGE,"E12"),sQuery(id+"F0.wireOp",EDGE,"E13"),sQuery(id+"F0.wireOp",EDGE,"E14"),sQuery(id+"F0.wireOp",EDGE,"E15"),sQuery(id+"F0.wireOp",EDGE,"E17.filletArc"),sQuery(id+"F0.wireOp",EDGE,"E18.filletArc"),sQuery(id+"F0.wireOp",EDGE,"E19.filletArc"),sQuery(id+"F0.wireOp",EDGE,"E20.filletArc"),sQuery(id+"F0.wireOp",EDGE,"E25.0"),sQuery(id+"F0.wireOp",EDGE,"E25.1"),sQuery(id+"F0.wireOp",EDGE,"E25.2"),sQuery(id+"F0.wireOp",EDGE,"E25.3"),sQuery(id+"F0.wireOp",EDGE,"E25.4"),sQuery(id+"F0.wireOp",EDGE,"E25.5"),sQuery(id+"F0.wireOp",EDGE,"E25.6"),sQuery(id+"F0.wireOp",EDGE,"E25.7")])],"isStart":false});
            extrude(context, id + "F17", {"entities" : qUnion([Q0, Q1, Q2]), "endBound" : BoundingType.UP_TO_SURFACE, "endBoundEntityFace" : qUnion([Q3]), "depth" : 25 * mm});
        }
    });
